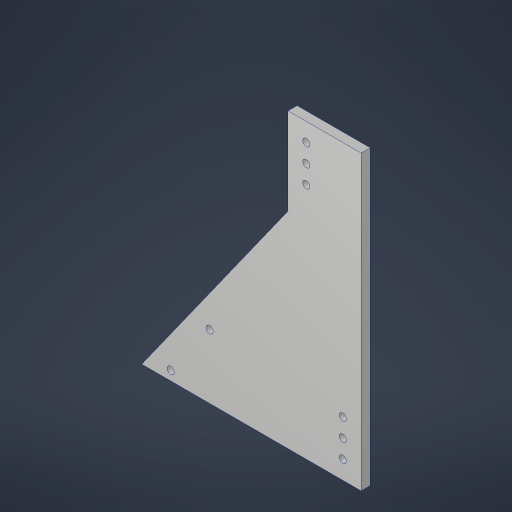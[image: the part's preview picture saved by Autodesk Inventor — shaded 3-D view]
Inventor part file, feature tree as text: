
AUTODESK INVENTOR PART (.ipt)
format: ipt  version: 2023.4 (Build 274418000, 418)  size: 252,416 bytes
history: native  units: in
note: dims shown in document units (in); Inventor stores cm internally (conversion verified against a paired STEP export)
features: sketch x4, projected_geometry x4, extrude x2, hole x2
ambient origin geometry x8: Origin, YZ Plane, XZ Plane, XY Plane, X Axis, Y Axis, Z Axis, Center Point
bodies: Solid1 (feature_tree)
feature tree (12):
  extrude  "Extrusion1"  Depth=1.0in
  hole  "Hole1"  [1 undecoded]
  sketch  "Sketch3"  dims[d5=0.5in d6=0.5in]
  extrude  "Extrusion2"  Depth=0.5in
  hole  "Hole2"  [1 undecoded]
  sketch  "Sketch2"  dims[d3=0.0in d4=1.0in]
  sketch  "Sketch4"  dims[d7=0.5in d8=0.5in]
  sketch  "Sketch5"  dims[d9=0.5in d10=0.5in d11=1.0in d12=0.201in d13=0.75in d14=0.385in d15=0.25in d16=0.5635in d17=1.0in d18=0.8108in d19=0.25in d20=0.125in d21=0.125in d22=0.25in d23=0.25in d24=0.25in d25=0.25in d26=0.25in d27=0.25in d28=0.125in d29=0.125in d30=0.125in d31=0.125in d32=2.0in d33=6.0in d34=1.0in d35=0.0in d36=0.375in d37=0.375in d38=0.5in d39=1.0in d40=0.201in d41=0.75in d42=0.375in d43=0.25in d44=0.5635in d45=1.0in d46=0.8108in d47=2.375in d48=10.0in d49=2.0in d50=0.0625in d51=0.378in d52=0.5in]
  projected_geometry  "Projected Loop1"
  projected_geometry  "Project Cut Edges1"
  projected_geometry  "Project Cut Edges2"
  projected_geometry  "Project Cut Edges3"
note: 2 required parameter values undecoded (feature->parameter linkage not recoverable at this tier; creation-order binding heuristic only, values carry confidence <= 0.55)
